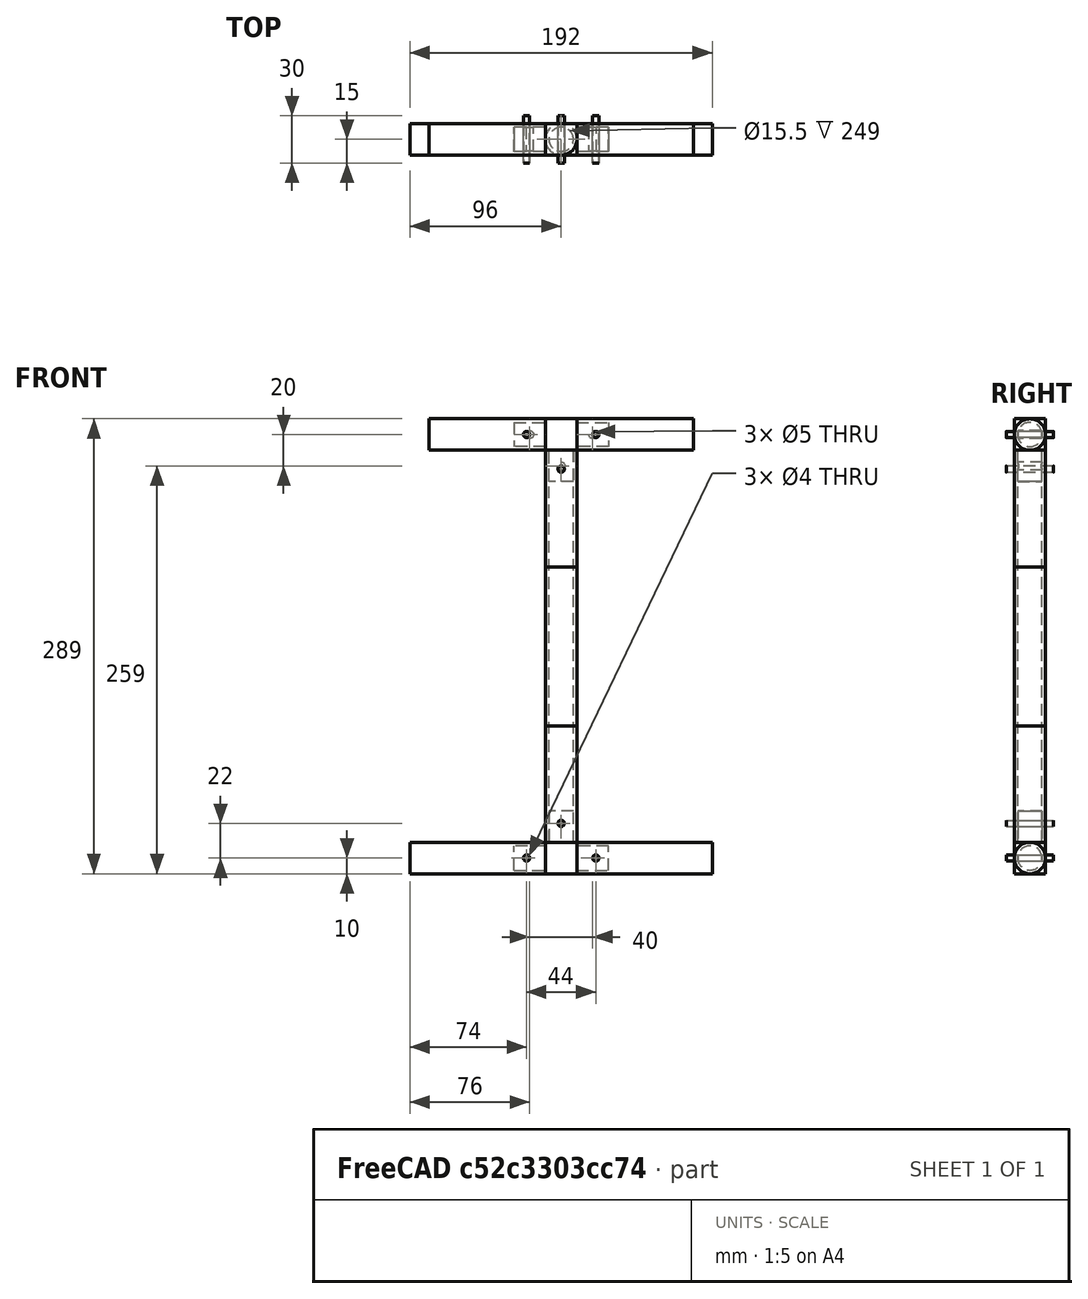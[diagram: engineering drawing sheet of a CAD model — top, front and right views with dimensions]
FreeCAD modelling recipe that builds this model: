
FCSTD DOCUMENT  (FreeCAD 0.21R33771 (Git))
Label: Torso_v1
License: All rights reserved
LicenseURL: http://en.wikipedia.org/wiki/All_rights_reserved
objects: Part::Cylinder×23, Part::MultiFuse×6, App::DocumentObjectGroup×3, Part::Box×2, Part::Cut×2, Part::FeaturePython×1
note: 34 computed .brp shape members not serialized (recipe doc carries the construction recipe); baked Part::Feature solids carry a one-line shape summary decoded from their .brp

FEATURE [Part::Cylinder] Cylinder  label="Cadera_izquierda"
  Angle = 360
  AttacherType = Attacher::AttachEngine3D
  FirstAngle = 0
  Height = 86
  Placement = pos=(10,0,0) rot=(0,1,0;1.5708rad)
  Radius = 10
  SecondAngle = 0
FEATURE [Part::Cylinder] Cylinder002  label="Cadera_dercha"
  Angle = 360
  AttacherType = Attacher::AttachEngine3D
  FirstAngle = 0
  Height = 86
  Placement = pos=(-96,0,0) rot=(0,1,0;1.5708rad)
  Radius = 10
  SecondAngle = 0
FEATURE [Part::Cylinder] Cylinder003  label="Clavicula_derecha"
  Angle = 360
  AttacherType = Attacher::AttachEngine3D
  FirstAngle = 0
  Height = 74
  Placement = pos=(-84,0,269) rot=(0,1,0;1.5708rad)
  Radius = 10
  SecondAngle = 0
FEATURE [Part::Cylinder] Cylinder004  label="Clavicula_izquierda"
  Angle = 360
  AttacherType = Attacher::AttachEngine3D
  FirstAngle = 0
  Height = 74
  Placement = pos=(10,0,269) rot=(0,1,0;1.5708rad)
  Radius = 10
  SecondAngle = 0
FEATURE [Part::Cylinder] Cylinder005  label="Vertebral001"
  Angle = 360
  AttacherType = Attacher::AttachEngine3D
  FirstAngle = 0
  Height = 74
  Placement = pos=(0,0,185) rot=(0,0,1;0rad)
  Radius = 10
  SecondAngle = 0
FEATURE [Part::Cylinder] Cylinder006  label="Vertebral002"
  Angle = 360
  AttacherType = Attacher::AttachEngine3D
  FirstAngle = 0
  Height = 101
  Placement = pos=(0,0,84) rot=(0,0,1;0rad)
  Radius = 10
  SecondAngle = 0
FEATURE [Part::Cylinder] Cylinder007  label="Vertebral003"
  Angle = 360
  AttacherType = Attacher::AttachEngine3D
  FirstAngle = 0
  Height = 74
  Placement = pos=(0,0,10) rot=(0,0,1;0rad)
  Radius = 10
  SecondAngle = 0
FEATURE [Part::Cylinder] Cylinder008  label="Ligamento_cadera"
  Angle = 360
  AttacherType = Attacher::AttachEngine3D
  FirstAngle = 0
  Height = 60
  Placement = pos=(-30,0,0) rot=(0,1,0;1.5708rad)
  Radius = 7.75
  SecondAngle = 0
FEATURE [Part::Cylinder] Cylinder009  label="Ligamento_cadera001"
  Angle = 360
  AttacherType = Attacher::AttachEngine3D
  FirstAngle = 0
  Height = 30
  Radius = 7.75
  SecondAngle = 0
FEATURE [Part::Box] Box  label="Cubo"
  AttacherType = Attacher::AttachEngine3D
  Height = 20
  Length = 20
  Placement = pos=(-10,-10,-10) rot=(0,0,1;0rad)
  Width = 20
FEATURE [Part::FeaturePython] Tube  label="Columna_vertebral"  # WARN: FeaturePython — macro-defined, semantics opaque (R4)
  AttacherType = Attacher::AttachEngine3D
  Height = 249
  InnerRadius = 7.75
  OuterRadius = 10
  Placement = pos=(0,0,10) rot=(0,0,1;0rad)
FEATURE [App::DocumentObjectGroup] Group  label="Tubo_PVC"
  Group = -> [Cylinder,Cylinder002,Cylinder003,Cylinder004,Cylinder005,Cylinder006,Cylinder007,Tube]
FEATURE [Part::Cylinder] Cylinder012  label="Taladros"
  Angle = 360
  AttacherType = Attacher::AttachEngine3D
  FirstAngle = 0
  Height = 30
  Placement = pos=(22,15,0) rot=(1,0,0;1.5708rad)
  Radius = 2
  SecondAngle = 0
FEATURE [Part::Cylinder] Cylinder013  label="Taladros001"
  Angle = 360
  AttacherType = Attacher::AttachEngine3D
  FirstAngle = 0
  Height = 30
  Placement = pos=(-22,15,0) rot=(1,0,0;1.5708rad)
  Radius = 2
  SecondAngle = 0
FEATURE [Part::Cylinder] Cylinder014  label="Taladros002"
  Angle = 360
  AttacherType = Attacher::AttachEngine3D
  FirstAngle = 0
  Height = 30
  Placement = pos=(0,15,22) rot=(1,0,0;1.5708rad)
  Radius = 2
  SecondAngle = 0
FEATURE [Part::MultiFuse] Fusion001  label="Ligamento_T"
  Shapes = -> [Box,Cylinder009,Cylinder008]
FEATURE [Part::MultiFuse] Fusion002  label="Taladros_ligamento_T"
  Shapes = -> [Cylinder014,Cylinder012,Cylinder013]
FEATURE [Part::Cut] Cut  label="Ligamento_T_imprimir"
  Base = -> Fusion001
  Tool = -> Fusion002
FEATURE [App::DocumentObjectGroup] Group001  label="Ligamento_T_cadera"
  Group = -> [Cut]
FEATURE [Part::Box] Box001  label="Cubo001"
  AttacherType = Attacher::AttachEngine3D
  Height = 20
  Length = 20
  Placement = pos=(-10,-10,-10) rot=(0,0,1;0rad)
  Width = 20
FEATURE [Part::Cylinder] Cylinder015  label="Ligamento_cadera002"
  Angle = 360
  AttacherType = Attacher::AttachEngine3D
  FirstAngle = 0
  Height = 60
  Placement = pos=(-30,0,0) rot=(0,1,0;1.5708rad)
  Radius = 7.75
  SecondAngle = 0
FEATURE [Part::Cylinder] Cylinder016  label="Ligamento_cadera003"
  Angle = 360
  AttacherType = Attacher::AttachEngine3D
  FirstAngle = 0
  Height = 30
  Radius = 7.75
  SecondAngle = 0
FEATURE [Part::Cylinder] Cylinder017  label="Taladros003"
  Angle = 360
  AttacherType = Attacher::AttachEngine3D
  FirstAngle = 0
  Height = 30
  Placement = pos=(20,15,0) rot=(1,0,0;1.5708rad)
  Radius = 2.5
  SecondAngle = 0
FEATURE [Part::Cylinder] Cylinder018  label="Taladros004"
  Angle = 360
  AttacherType = Attacher::AttachEngine3D
  FirstAngle = 0
  Height = 30
  Placement = pos=(-20,15,0) rot=(1,0,0;1.5708rad)
  Radius = 2.5
  SecondAngle = 0
FEATURE [Part::Cylinder] Cylinder019  label="Taladros005"
  Angle = 360
  AttacherType = Attacher::AttachEngine3D
  FirstAngle = 0
  Height = 30
  Placement = pos=(0,15,20) rot=(1,0,0;1.5708rad)
  Radius = 2.5
  SecondAngle = 0
FEATURE [Part::MultiFuse] Fusion003  label="Ligamento_T001"
  Shapes = -> [Box001,Cylinder016,Cylinder015]
FEATURE [Part::MultiFuse] Fusion004  label="Taladros_ligamento_T001"
  Shapes = -> [Cylinder019,Cylinder017,Cylinder018]
FEATURE [Part::Cut] Cut001  label="Ligamento_T_imprimir001"
  Base = -> Fusion003
  Placement = pos=(0,0,269) rot=(1,0,0;3.14159rad)
  Tool = -> Fusion004
FEATURE [App::DocumentObjectGroup] Group002  label="Ligamento_T_clavicula"
  Group = -> [Cut001]
FEATURE [Part::Cylinder] Cylinder020  label="Taladros006"
  Angle = 360
  AttacherType = Attacher::AttachEngine3D
  FirstAngle = 0
  Height = 30
  Placement = pos=(22,15,0) rot=(1,0,0;1.5708rad)
  Radius = 2
  SecondAngle = 0
FEATURE [Part::Cylinder] Cylinder021  label="Taladros007"
  Angle = 360
  AttacherType = Attacher::AttachEngine3D
  FirstAngle = 0
  Height = 30
  Placement = pos=(-22,15,0) rot=(1,0,0;1.5708rad)
  Radius = 2
  SecondAngle = 0
FEATURE [Part::Cylinder] Cylinder022  label="Taladros008"
  Angle = 360
  AttacherType = Attacher::AttachEngine3D
  FirstAngle = 0
  Height = 30
  Placement = pos=(0,15,22) rot=(1,0,0;1.5708rad)
  Radius = 2
  SecondAngle = 0
FEATURE [Part::MultiFuse] Fusion005  label="Taladros_ligamento_T002"
  Shapes = -> [Cylinder022,Cylinder020,Cylinder021]
FEATURE [Part::Cylinder] Cylinder023  label="Taladros009"
  Angle = 360
  AttacherType = Attacher::AttachEngine3D
  FirstAngle = 0
  Height = 30
  Placement = pos=(22,15,0) rot=(1,0,0;1.5708rad)
  Radius = 2
  SecondAngle = 0
FEATURE [Part::Cylinder] Cylinder024  label="Taladros010"
  Angle = 360
  AttacherType = Attacher::AttachEngine3D
  FirstAngle = 0
  Height = 30
  Placement = pos=(-22,15,0) rot=(1,0,0;1.5708rad)
  Radius = 2
  SecondAngle = 0
FEATURE [Part::Cylinder] Cylinder025  label="Taladros011"
  Angle = 360
  AttacherType = Attacher::AttachEngine3D
  FirstAngle = 0
  Height = 30
  Placement = pos=(0,15,22) rot=(1,0,0;1.5708rad)
  Radius = 2
  SecondAngle = 0
FEATURE [Part::MultiFuse] Fusion006  label="Taladros_ligamento_T003"
  Placement = pos=(0,0,269) rot=(1,0,0;3.14159rad)
  Shapes = -> [Cylinder025,Cylinder023,Cylinder024]
